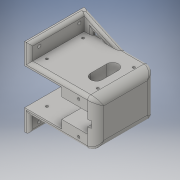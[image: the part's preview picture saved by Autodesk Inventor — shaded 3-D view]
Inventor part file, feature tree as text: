
AUTODESK INVENTOR PART (.ipt)
format: ipt  version: 2016 (Build 200138000, 138)  size: 465,408 bytes
history: native  units: in
note: dims shown in document units (in); Inventor stores cm internally (conversion verified against a paired STEP export)
features: sketch x21, extrude x13, hole x5, plane x3, fillet x2, rib x1
ambient origin geometry x8: Origin, YZ Plane, XZ Plane, XY Plane, X Axis, Y Axis, Z Axis, Center Point
bodies: Solid1 (feature_tree)
feature tree (45):
  extrude  "Extrusion1"  Depth=1.4488in
  extrude  "Extrusion2"  Depth=0.1181in
  sketch  "Sketch3"  dims[d6=0.1181in d7=0.8819in d8=0.0in]
  plane  "Work Plane1"
  extrude  "Extrusion3"  Depth=0.8819in TaperAngle=0.0deg
  sketch  "Sketch6"  dims[d12=1.1339in d13=0.128in]
  extrude  "Extrusion4"  Depth=0.1181in
  sketch  "Sketch8"  dims[d16=0.128in d17=0.128in]
  plane  "Work Plane2"
  extrude  "Extrusion5"  Depth=0.128in
  extrude  "Extrusion6"  Depth=0.128in
  plane  "Work Plane3"
  rib  "Rib1"
  sketch  "Sketch11"  dims[d31=0.3937in d32=0.0in d33=0.3937in d34=0.0in]
  hole  "Hole2"  [1 undecoded]
  extrude  "Extrusion7"  Depth=0.128in
  extrude  "Extrusion8"  Depth=0.1181in TaperAngle=0.0deg
  extrude  "Extrusion9"  Depth=0.3937in TaperAngle=0.0deg
  hole  "Hole3"  [1 undecoded]
  extrude  "Extrusion10"  Depth=0.8661in
  extrude  "Extrusion11"  Depth=0.1181in
  hole  "Hole4"  [1 undecoded]
  hole  "Hole5"  [1 undecoded]
  hole  "Hole6"  [1 undecoded]
  fillet  "Fillet2"  Radius=0.1575in
  fillet  "Fillet3"  Radius=0.1575in
  extrude  "Extrusion12"  Depth=0.2362in
  extrude  "Extrusion13"  Depth=0.0787in
  sketch  "Sketch1"  dims[d0=1.6102in d1=1.4488in]
  sketch  "Sketch2"  dims[d2=0.1181in d3=0.0in d5=0.1181in]
  sketch  "Sketch5"  dims[d9=0.1181in d10=0.0in d11=1.4921in]
  sketch  "Sketch7"  dims[d14=0.128in d15=0.128in]
  sketch  "Sketch9"  dims[d19=0.128in d20=0.128in]
  sketch  "Sketch10"  dims[d21=0.128in d29=0.1181in d30=0.0in]
  sketch  "Sketch12"  dims[d35=0.1181in d36=0.1181in]
  sketch  "Sketch13"  dims[d38=0.8661in d39=0.8661in]
  sketch  "Sketch14"  dims[d40=0.1969in d41=0.1181in d42=0.0in d43=0.0in d44=0.0394in d45=0.0394in d46=0.1181in]
  sketch  "Sketch15"  dims[d49=0.1181in d50=0.1181in]
  sketch  "Sketch16"  dims[d51=0.2362in d52=0.2362in]
  sketch  "Sketch17"  dims[d53=0.1575in d54=0.1575in d55=0.1575in d56=0.1575in]
  sketch  "Sketch18"  dims[d57=0.2362in d58=0.2362in]
  sketch  "Sketch19"  dims[d59=0.0787in d60=0.2362in d61=0.1575in d62=0.0787in d63=90.0deg d64=0.315in d65=0.8108in d66=0.1969in]
  sketch  "Sketch20"  dims[d67=0.1969in]
  sketch  "Sketch21"  dims[d68=0.1575in]
  sketch  "Sketch22"  dims[d69=0.3622in d70=0.3622in d71=0.0787in d72=0.0in d73=0.2362in d74=0.0in d75=0.0787in d76=0.3937in d77=0.0in d78=0.4409in d79=0.4409in d80=0.0984in d81=0.0984in d82=0.0591in d83=0.2362in d84=0.1575in d85=0.0787in d86=90.0deg d87=0.1969in d88=0.8108in d89=0.0787in d90=90.0deg d91=0.2047in d92=0.0in d93=0.0787in d94=90.0deg d95=0.2047in d96=0.0in d97=0.1024in d98=0.1024in d99=1.1614in d100=1.1614in d101=0.1024in d102=0.1024in d103=0.0591in d104=0.2362in d105=0.1575in d106=0.0787in d107=90.0deg d108=0.1969in d109=0.8108in d110=0.4134in d111=0.4134in d112=0.4134in d113=0.4134in d114=0.1614in d115=0.1614in d116=0.1614in d117=0.1614in d118=0.0591in d119=0.2362in d120=0.1575in d121=0.0787in d122=90.0deg d123=0.1969in d124=0.8108in d125=0.0591in d126=0.2362in d127=0.1575in d128=0.0787in d129=90.0deg d130=0.315in d131=0.8108in d132=0.0787in d133=0.1969in d134=0.6457in d135=0.6457in d136=0.315in d137=0.1969in d138=19.685in d139=0.0in d140=0.4803in d141=0.4803in d144=0.1969in d145=19.685in d146=0.0in d147=0.9843in]
note: 5 required parameter values undecoded (feature->parameter linkage not recoverable at this tier; creation-order binding heuristic only, values carry confidence <= 0.55)
